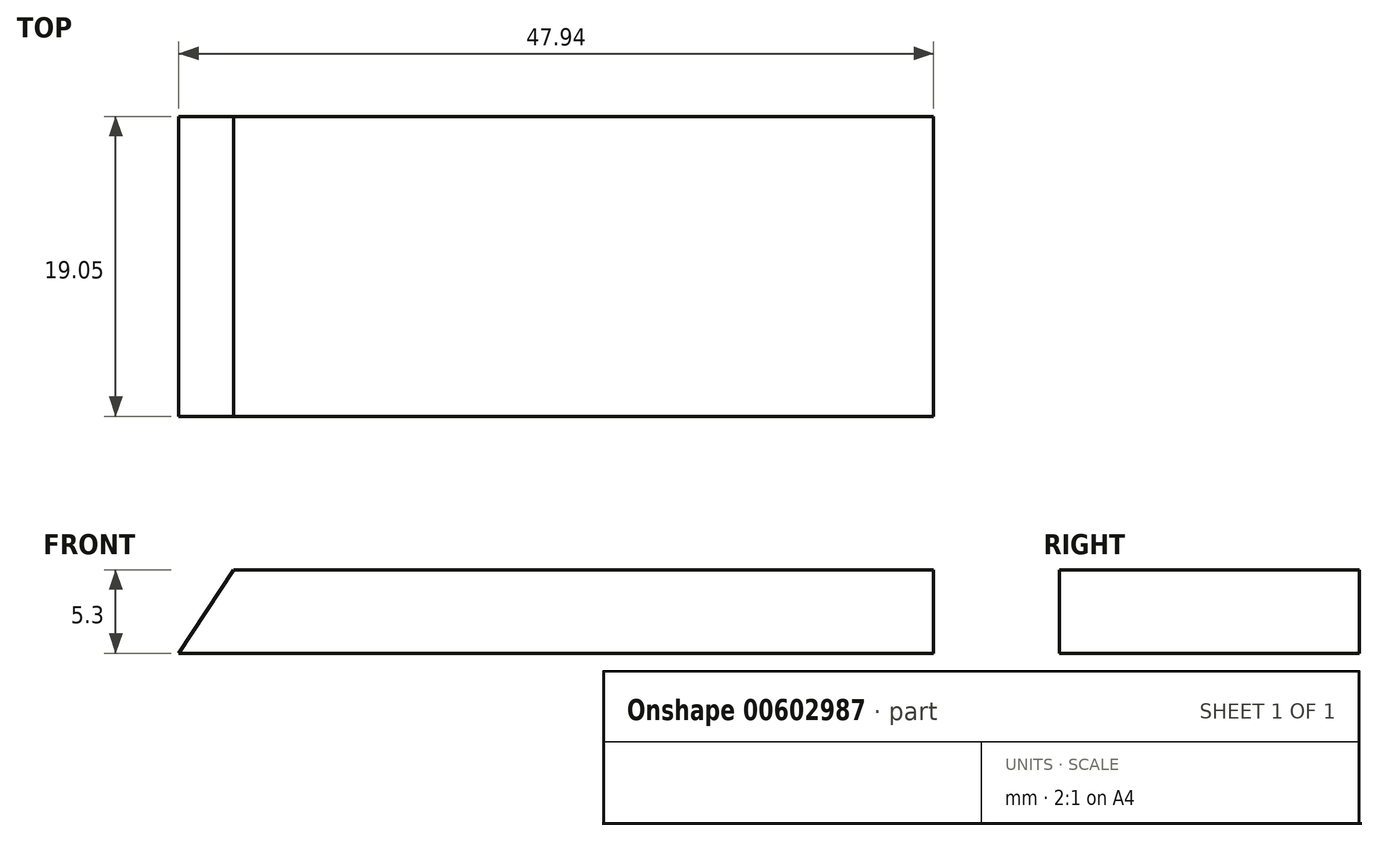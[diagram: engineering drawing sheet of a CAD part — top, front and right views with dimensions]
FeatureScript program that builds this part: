
annotation { "Feature Type Name" : "Feature", "Feature Type Description" : "" }
export const myFeature = defineFeature(function(context is Context, id is Id, definition is map)
    precondition{}
    {
        {
            var Q0;
            Q0=qCreatedBy(makeId("Front.planeOp"),FACE);
            var sketch = newSketch(context, id + "F0", { "sketchPlane" : qUnion([Q0])});
            skLineSegment(sketch, "E0", {"start": v(0, 0) * mm, "end": v(3.5, 5.3) * mm});
            skLineSegment(sketch, "E1", {"start": v(3.5, 5.3) * mm, "end": v(47.94, 5.3) * mm});
            skLineSegment(sketch, "E2", {"start": v(47.94, 5.3) * mm, "end": v(47.94, 0) * mm});
            skLineSegment(sketch, "E3", {"start": v(47.94, 0) * mm, "end": v(0, 0) * mm});
            skSolve(sketch);
        }
        {
            var Q0;
            Q0=makeQuery(id+"F0.imprint","IMPRINT",FACE,{"disambiguationData":[TD([[makeQuery(id+"F0.imprint","IMPRINT",EDGE,{"derivedFrom":sQuery(id+"F0.wireOp",EDGE,"E0")}),-1.0]])]});
            extrude(context, id + "F1", {"entities" : qUnion([Q0]), "depth" : 19.05 * mm, "offsetDistance" : 25.4 * mm});
        }
    });
